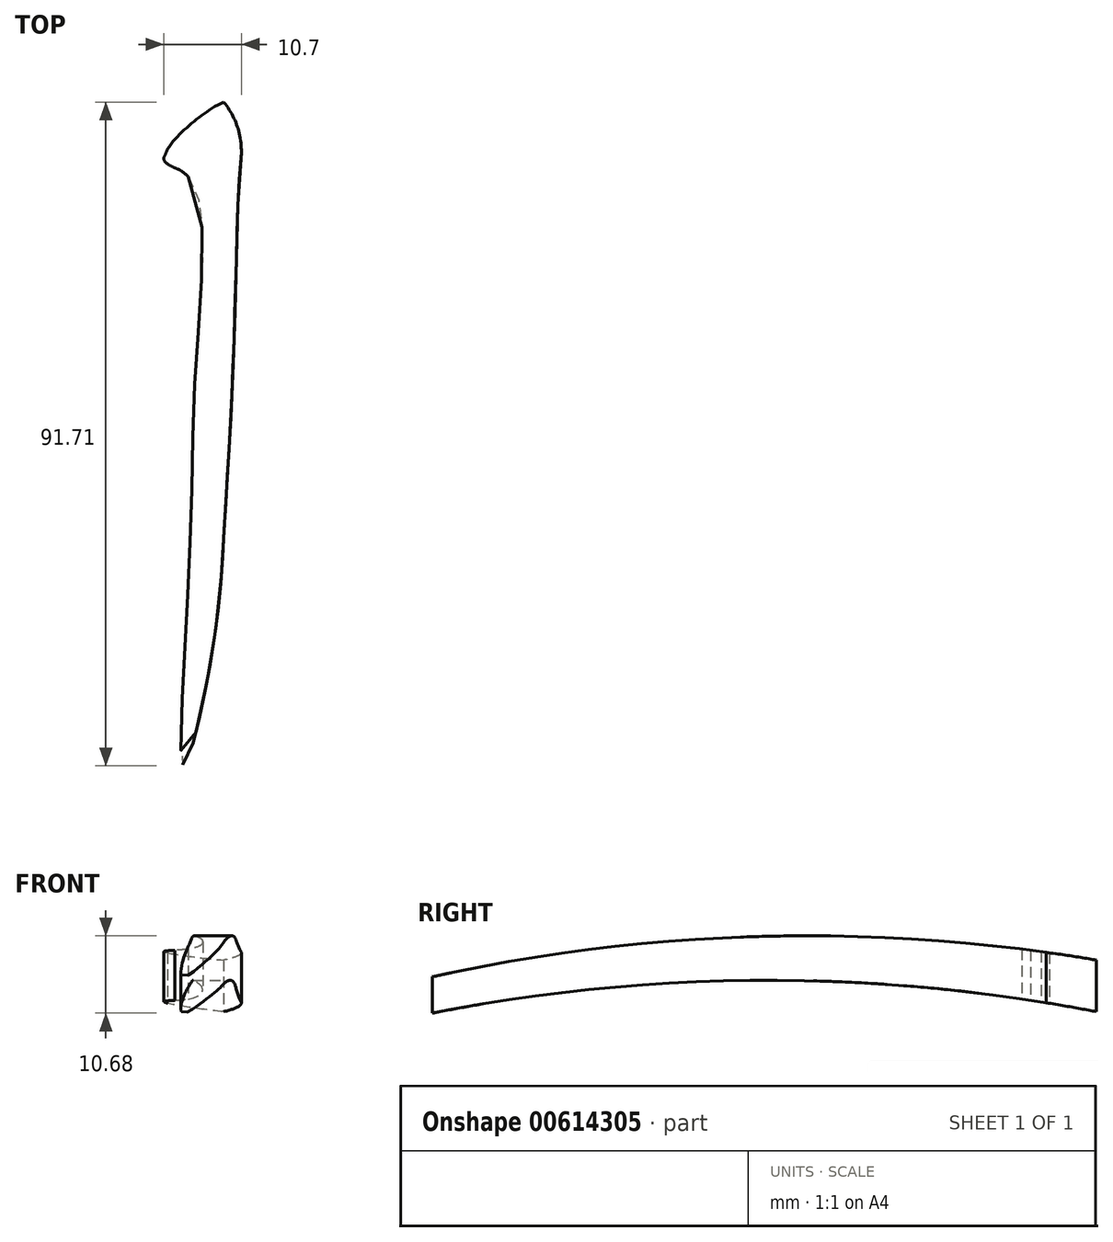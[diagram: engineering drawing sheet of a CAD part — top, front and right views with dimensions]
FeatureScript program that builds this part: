
annotation { "Feature Type Name" : "Feature", "Feature Type Description" : "" }
export const myFeature = defineFeature(function(context is Context, id is Id, definition is map)
    precondition{}
    {
        {
            var Q0;
            Q0=qCreatedBy(makeId("Right.planeOp"),FACE);
            var sketch = newSketch(context, id + "F0", { "sketchPlane" : qUnion([Q0])});
            skArc(sketch, "E0", {"start": v(55.06, 0) * mm, "mid": v(2.56, 5.82) * mm, "end": v(-49.94, 0) * mm});
            skArc(sketch, "E1", {"start": v(50.06, -6.24) * mm, "mid": v(0.12, -0.35) * mm, "end": v(-49.94, -5) * mm});
            skSolve(sketch);
        }
        {
            var Q0;
            Q0 = qSketchRegion(id + "F0", true);
            var Q1;
            Q1=sQuery(id+"F0.wireOp",EDGE,"E0");
            extrude(context, id + "F1", {"entities" : qUnion([Q0]), "bodyType" : ToolBodyType.SURFACE, "surfaceEntities" : qUnion([Q1]), "endBound" : BoundingType.SYMMETRIC, "depth" : 30 * mm, "offsetDistance" : 25 * mm});
        }
        {
            var Q0;
            Q0=sQuery(id+"F0.wireOp",EDGE,"E1");
            extrude(context, id + "F2", {"bodyType" : ToolBodyType.SURFACE, "surfaceEntities" : qUnion([Q0]), "endBound" : BoundingType.SYMMETRIC, "depth" : 30 * mm, "offsetDistance" : 25 * mm});
        }
        {
            var Q0;
            Q0=qCreatedBy(makeId("Top.planeOp"),FACE);
            var sketch = newSketch(context, id + "F3", { "sketchPlane" : qUnion([Q0])});
            skFitSpline(sketch, "E2", {"points": [v(9.57, 42.83) * mm, v(10.7, 35.54) * mm, v(9.65, 8.5) * mm, v(8.3, -17.31) * mm, v(6.47, -34.72) * mm, v(2.71, -49.22) * mm, v(3.55, -20.34) * mm, v(4.49, 7.58) * mm, v(3.36, 32.17) * mm, v(0, 34.85) * mm, v(9.57, 42.83) * mm]});
            skArc(sketch, "E3", {"start": v(3.36, 32.17) * mm, "mid": v(0, 33.67) * mm, "end": v(-3.36, 32.17) * mm});
            skArc(sketch, "E4", {"start": v(10.7, 35.54) * mm, "mid": v(0.01, 46.4) * mm, "end": v(-10.7, 35.56) * mm});
            skFitSpline(sketch, "E5.trimOffspring", {"points": [v(-1.01, 49.33) * mm, v(-9.56, 42.85) * mm, v(-10.7, 35.56) * mm, v(-9.7, 8.52) * mm, v(-8.4, -17.3) * mm, v(-6.62, -34.7) * mm, v(-2.89, -49.21) * mm, v(-3.66, -20.33) * mm, v(-4.55, 7.59) * mm, v(-3.36, 32.17) * mm, v(0, 34.85) * mm, v(-1.01, 49.33) * mm]});
            skSolve(sketch);
        }
        {
            var Q0;
            Q0=makeQuery(id+"F3.imprint","IMPRINT",FACE,{"disambiguationData":[TD([[makeQuery(id+"F3.imprint","IMPRINT",EDGE,{"derivedFrom":sQuery(id+"F3.wireOp",EDGE,"E2")}),-1.0]])]});
            var Q1;
            Q1=makeQuery(id+"F3.imprint","IMPRINT",FACE,{"disambiguationData":[TD([[makeQuery(id+"F3.imprint","IMPRINT",EDGE,{"derivedFrom":sQuery(id+"F3.wireOp",EDGE,"qRvSCHHM-FeYE-0uNC-WrOf-UtnJRDfWNlrE")}),-1.0]])]});
            var Q2;
            Q2=makeQuery(id+"F1.opExtrude","SWEPT_FACE",FACE,{"disambiguationData":[OSD([sQuery(id+"F0.wireOp",EDGE,"E0")])]});
            extrude(context, id + "F4", {"entities" : qUnion([Q0, Q1]), "endBound" : BoundingType.UP_TO_SURFACE, "depth" : 25 * mm, "endBoundEntityFace" : qUnion([Q2]), "offsetDistance" : 25 * mm});
        }
        {
            var Q0;
            Q0=makeQuery(id+"F3.imprint","IMPRINT",FACE,{"disambiguationData":[TD([[makeQuery(id+"F3.imprint","IMPRINT",EDGE,{"derivedFrom":sQuery(id+"F3.wireOp",EDGE,"E2")}),-1.0]])]});
            var Q1;
            Q1=makeQuery(id+"F3.imprint","IMPRINT",FACE,{"disambiguationData":[TD([[makeQuery(id+"F3.imprint","IMPRINT",EDGE,{"derivedFrom":sQuery(id+"F3.wireOp",EDGE,"qRvSCHHM-FeYE-0uNC-WrOf-UtnJRDfWNlrE")}),-1.0]])]});
            var Q2;
            Q2=sQuery(id+"F3.wireOp",EDGE,"E2");
            var Q3;
            Q3=makeQuery(id+"F2.opExtrude","SWEPT_FACE",FACE,{"disambiguationData":[OSD([sQuery(id+"F0.wireOp",EDGE,"E1")])]});
            extrude(context, id + "F5", {"entities" : qUnion([Q0, Q1]), "operationType" : NewBodyOperationType.ADD, "surfaceEntities" : qUnion([Q2]), "endBound" : BoundingType.UP_TO_SURFACE, "oppositeDirection" : true, "depth" : 25 * mm, "endBoundEntityFace" : qUnion([Q3]), "offsetDistance" : 25 * mm});
        }
    });
